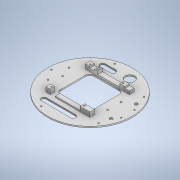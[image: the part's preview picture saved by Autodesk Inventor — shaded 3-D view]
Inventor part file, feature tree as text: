
AUTODESK INVENTOR PART (.ipt)
format: ipt  version: 2022 (Build 260153000, 153)  size: 321,024 bytes
history: native  units: mm
features: extrude x12, sketch x11
ambient origin geometry x8: Origin, YZ Plane, XZ Plane, XY Plane, X Axis, Y Axis, Z Axis, Center Point
bodies: Solid1 (feature_tree)
feature tree (23):
  extrude  "Extrusion1"  Depth=3.0mm TaperAngle=0.0deg
  extrude  "Extrusion2"  Depth=105.0mm
  extrude  "Extrusion3"  Depth=11.0mm
  extrude  "Extrusion4"  Depth=104.5mm
  extrude  "Extrusion5"  Depth=104.5mm
  extrude  "Extrusion6"  Depth=11.2mm TaperAngle=0.0deg
  extrude  "Extrusion7"  Depth=12.0mm
  extrude  "Extrusion8"  TaperAngle=0.0deg  [1 undecoded]
  extrude  "Extrusion9"  Depth=11.0mm TaperAngle=0.0deg
  extrude  "Extrusion10"  Depth=10.8mm
  extrude  "Extrusion12"  Depth=52.65mm
  extrude  "Extrusion14"  Depth=11.65mm
  sketch  "Sketch1"  dims[d0=200.0mm d9=3.0mm d10=0.0mm]
  sketch  "Sketch2"  dims[d23=4.0mm d24=0.0mm d25=105.0mm]
  sketch  "Sketch3"  dims[d26=52.5mm d27=11.0mm]
  sketch  "Sketch4"  dims[d28=11.0mm d29=104.5mm]
  sketch  "Sketch5"  dims[d30=104.5mm d31=52.25mm]
  sketch  "Sketch6"  dims[d32=52.25mm d33=11.2mm d34=0.0mm]
  sketch  "Sketch7"  dims[d35=10.25mm d36=12.0mm]
  sketch  "Sketch8"  dims[d37=59.0mm d38=0.0mm]
  sketch  "Sketch9"  dims[d39=2.75mm d40=11.0mm d41=0.0mm]
  sketch  "Sketch10"  dims[d42=10.15mm d43=10.8mm]
  sketch  "Sketch16"  dims[d44=8.25mm d45=52.65mm d46=11.65mm d47=7.3mm d48=4.0mm d49=7.25mm d51=11.0mm d52=11.0mm d53=0.0mm d54=30.0mm d55=30.0mm d56=80.0mm d57=80.0mm d58=7.0mm d59=7.0mm d63=11.0mm d64=0.0mm d65=4.0mm d66=2.125mm d67=2.0mm d68=2.0mm d69=0.0mm d70=19.5mm d71=6.5mm d72=3.5mm d73=19.5mm d74=6.5mm d75=3.5mm d76=6.5mm d77=6.5mm d78=6.5mm d79=6.5mm d80=3.5mm d81=3.5mm d82=18.2mm d83=0.0mm d84=12.0mm d86=70.0mm d87=40.0mm d88=70.0mm d89=70.0mm d90=12.0mm d91=4.0mm d92=0.0mm d94=50.0mm d95=75.0mm d96=3.5mm d97=3.5mm d98=11.0mm d99=0.0mm d107=12.0mm d108=11.2mm d109=0.0mm d111=22.5mm d112=20.0mm d113=15.0mm d114=70.0mm d115=75.0mm d120=25.0mm d121=75.0mm d127=80.0mm d128=40.0mm d129=80.0mm d130=40.0mm d131=10.0mm d132=3.5mm d133=65.0mm d134=25.0mm d135=3.5mm d136=92.0mm d137=50.0mm d139=360.0deg d141=40.0mm d142=40.0mm d143=20.0mm d144=3.0mm d146=4.0mm d147=4.0mm d148=4.0mm d149=4.0mm d150=4.0mm d151=4.0mm d152=4.0mm d153=4.0mm d154=3.5mm d155=3.5mm d156=3.5mm d157=3.5mm d158=10.0mm d159=0.0mm d160=25.0mm d161=12.0mm d162=54.0mm d100=0.5mm d101=0.872665mm d102=0.5mm d103=0.872665mm]
note: 1 required parameter value undecoded (feature->parameter linkage not recoverable at this tier; creation-order binding heuristic only, values carry confidence <= 0.55)
